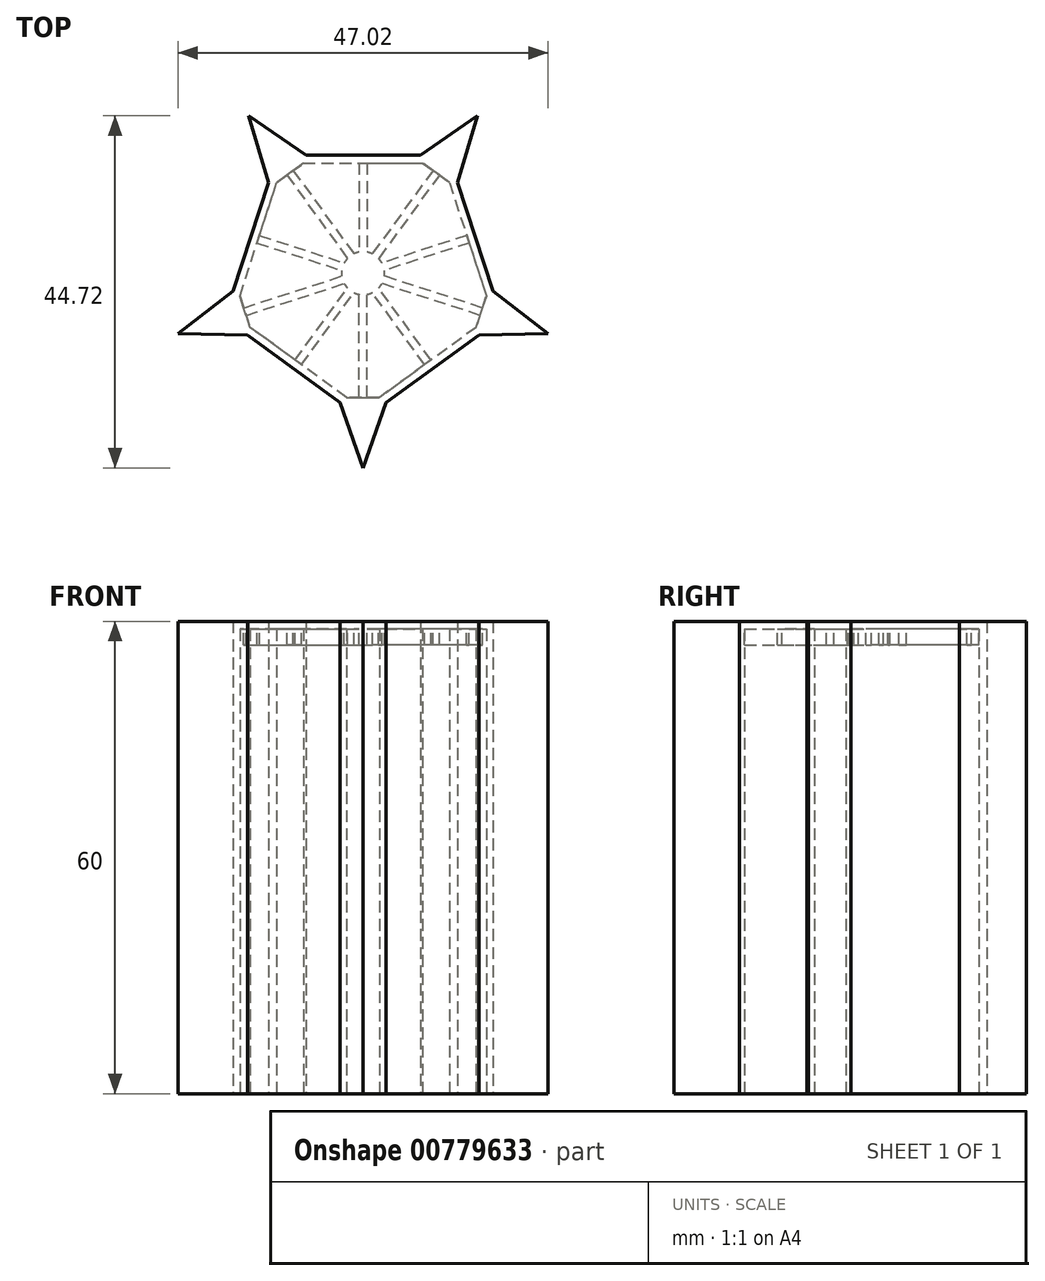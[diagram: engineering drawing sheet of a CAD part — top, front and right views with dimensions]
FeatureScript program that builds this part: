
annotation { "Feature Type Name" : "Feature", "Feature Type Description" : "" }
export const myFeature = defineFeature(function(context is Context, id is Id, definition is map)
    precondition{}
    {
        {
            var Q0;
            Q0=qCreatedBy(makeId("Top.planeOp"),FACE);
            var sketch = newSketch(context, id + "F0", { "sketchPlane" : qUnion([Q0])});
            skCircle(sketch, "E0.cCircle", {"center": v(0, 0) * mm, "radius": 20 * mm, "construction": true});
            skLineSegment(sketch, "E0.0", {"start": v(-14.53, 20) * mm, "end": v(14.53, 20) * mm, "construction": true});
            skLineSegment(sketch, "E0.1", {"start": v(14.53, 20) * mm, "end": v(23.51, -7.64) * mm, "construction": true});
            skLineSegment(sketch, "E0.2", {"start": v(23.51, -7.64) * mm, "end": v(0, -24.72) * mm, "construction": true});
            skLineSegment(sketch, "E0.3", {"start": v(0, -24.72) * mm, "end": v(-23.51, -7.64) * mm, "construction": true});
            skLineSegment(sketch, "E0.4", {"start": v(-23.51, -7.64) * mm, "end": v(-14.53, 20) * mm, "construction": true});
            skPoint(sketch, "E0.0.midPoint", {"position": v(0, 20) * mm});
            skLineSegment(sketch, "E1", {"start": v(-14.53, 20) * mm, "end": v(0, 0) * mm, "construction": true});
            skLineSegment(sketch, "E2", {"start": v(14.53, 20) * mm, "end": v(0, 0) * mm, "construction": true});
            skLineSegment(sketch, "E3", {"start": v(23.51, -7.64) * mm, "end": v(0, 0) * mm, "construction": true});
            skLineSegment(sketch, "E4", {"start": v(0, -24.72) * mm, "end": v(0, 0) * mm, "construction": true});
            skLineSegment(sketch, "E5", {"start": v(-23.51, -7.64) * mm, "end": v(0, 0) * mm, "construction": true});
            skCircle(sketch, "E6.cCircle", {"center": v(0, 0) * mm, "radius": 10 * mm, "construction": true});
            skLineSegment(sketch, "E6.0", {"start": v(-7.27, 10) * mm, "end": v(7.27, 10) * mm, "construction": true});
            skLineSegment(sketch, "E6.1", {"start": v(7.27, 10) * mm, "end": v(11.76, -3.82) * mm, "construction": true});
            skLineSegment(sketch, "E6.2", {"start": v(11.76, -3.82) * mm, "end": v(0, -12.36) * mm, "construction": true});
            skLineSegment(sketch, "E6.3", {"start": v(0, -12.36) * mm, "end": v(-11.76, -3.82) * mm, "construction": true});
            skLineSegment(sketch, "E6.4", {"start": v(-11.76, -3.82) * mm, "end": v(-7.27, 10) * mm, "construction": true});
            skPoint(sketch, "E6.0.midPoint", {"position": v(0, 10) * mm});
            skLineSegment(sketch, "E7", {"start": v(-14.53, 20) * mm, "end": v(-9.51, 3.1) * mm});
            skLineSegment(sketch, "E8", {"start": v(-9.51, 3.1) * mm, "end": v(-23.51, -7.64) * mm});
            skLineSegment(sketch, "E9", {"start": v(-14.53, 20) * mm, "end": v(0, 10) * mm});
            skLineSegment(sketch, "E10", {"start": v(14.53, 20) * mm, "end": v(0, 10) * mm});
            skLineSegment(sketch, "E11", {"start": v(14.53, 20) * mm, "end": v(9.51, 3.1) * mm});
            skLineSegment(sketch, "E12", {"start": v(9.51, 3.1) * mm, "end": v(23.51, -7.64) * mm});
            skLineSegment(sketch, "E13", {"start": v(23.51, -7.64) * mm, "end": v(5.88, -8.1) * mm});
            skLineSegment(sketch, "E14", {"start": v(5.88, -8.1) * mm, "end": v(0, -24.72) * mm});
            skLineSegment(sketch, "E15", {"start": v(-23.51, -7.64) * mm, "end": v(-5.88, -8.1) * mm});
            skLineSegment(sketch, "E16", {"start": v(-5.88, -8.1) * mm, "end": v(0, -24.72) * mm});
            skCircle(sketch, "E17.cCircle", {"center": v(0, 0) * mm, "radius": 15 * mm, "construction": true});
            skLineSegment(sketch, "E17.0", {"start": v(-10.9, 15) * mm, "end": v(10.9, 15) * mm});
            skLineSegment(sketch, "E17.1", {"start": v(10.9, 15) * mm, "end": v(17.63, -5.73) * mm});
            skLineSegment(sketch, "E17.2", {"start": v(17.63, -5.73) * mm, "end": v(0, -18.54) * mm});
            skLineSegment(sketch, "E17.3", {"start": v(0, -18.54) * mm, "end": v(-17.63, -5.73) * mm});
            skLineSegment(sketch, "E17.4", {"start": v(-17.63, -5.73) * mm, "end": v(-10.9, 15) * mm});
            skPoint(sketch, "E17.0.midPoint", {"position": v(0, 15) * mm});
            skPoint(sketch, "E18", {"position": v(7.27, 15) * mm});
            skSolve(sketch);
        }
        {
            var Q0;
            Q0 = qSketchRegion(id + "F0", true);
            extrude(context, id + "F1", {"entities" : qUnion([Q0]), "depth" : 60 * mm, "offsetDistance" : 25 * mm});
        }
        {
            var Q0;
            Q0=makeQuery(id+"F1.opExtrude","CAP_FACE",FACE,{"disambiguationData":[OSD([sQuery(id+"F0.wireOp",EDGE,"E7"),sQuery(id+"F0.wireOp",EDGE,"E8"),sQuery(id+"F0.wireOp",EDGE,"E9"),sQuery(id+"F0.wireOp",EDGE,"E10"),sQuery(id+"F0.wireOp",EDGE,"E11"),sQuery(id+"F0.wireOp",EDGE,"E12"),sQuery(id+"F0.wireOp",EDGE,"E13"),sQuery(id+"F0.wireOp",EDGE,"E14"),sQuery(id+"F0.wireOp",EDGE,"E15"),sQuery(id+"F0.wireOp",EDGE,"E16"),sQuery(id+"F0.wireOp",EDGE,"E17.0"),sQuery(id+"F0.wireOp",EDGE,"E17.1"),sQuery(id+"F0.wireOp",EDGE,"E17.2"),sQuery(id+"F0.wireOp",EDGE,"E17.3"),sQuery(id+"F0.wireOp",EDGE,"E17.4")])],"isStart":true});
            shell(context, id + "F2", {"entities" : qUnion([Q0]), "thickness" : 1 * mm});
        }
        {
            var Q0;
            Q0=makeQuery(id+"F2.opShell","OFFSET_FACE",FACE,{"disambiguationData":[OSD([sQuery(id+"F0.wireOp",EDGE,"E7"),sQuery(id+"F0.wireOp",EDGE,"E8"),sQuery(id+"F0.wireOp",EDGE,"E9"),sQuery(id+"F0.wireOp",EDGE,"E10"),sQuery(id+"F0.wireOp",EDGE,"E11"),sQuery(id+"F0.wireOp",EDGE,"E12"),sQuery(id+"F0.wireOp",EDGE,"E13"),sQuery(id+"F0.wireOp",EDGE,"E14"),sQuery(id+"F0.wireOp",EDGE,"E15"),sQuery(id+"F0.wireOp",EDGE,"E16"),sQuery(id+"F0.wireOp",EDGE,"E17.0"),sQuery(id+"F0.wireOp",EDGE,"E17.1"),sQuery(id+"F0.wireOp",EDGE,"E17.2"),sQuery(id+"F0.wireOp",EDGE,"E17.3"),sQuery(id+"F0.wireOp",EDGE,"E17.4")])]});
            var sketch = newSketch(context, id + "F3", { "sketchPlane" : qUnion([Q0])});
            skLineSegment(sketch, "E19.0", {"start": v(-2.1, 15.78) * mm, "end": v(-14.36, 6.87) * mm});
            skLineSegment(sketch, "E20.0", {"start": v(14.36, 6.87) * mm, "end": v(2.1, 15.78) * mm});
            skLineSegment(sketch, "E21.0", {"start": v(10.97, -11.53) * mm, "end": v(15.66, 2.88) * mm});
            skLineSegment(sketch, "E22.0", {"start": v(-7.58, -14) * mm, "end": v(7.58, -14) * mm});
            skLineSegment(sketch, "E23.0", {"start": v(-15.66, 2.88) * mm, "end": v(-10.97, -11.53) * mm});
            skLineSegment(sketch, "E24", {"start": v(-14.36, 6.87) * mm, "end": v(-15.66, 2.88) * mm});
            skLineSegment(sketch, "E25", {"start": v(-2.1, 15.78) * mm, "end": v(2.1, 15.78) * mm});
            skLineSegment(sketch, "E26", {"start": v(14.36, 6.87) * mm, "end": v(15.66, 2.88) * mm});
            skLineSegment(sketch, "E27", {"start": v(10.97, -11.53) * mm, "end": v(7.58, -14) * mm});
            skLineSegment(sketch, "E28", {"start": v(-7.58, -14) * mm, "end": v(-10.97, -11.53) * mm});
            skSolve(sketch);
        }
        {
            var Q0;
            Q0=makeQuery(id+"F3.imprint","IMPRINT",FACE,{"disambiguationData":[TD([[makeQuery(id+"F3.imprint","IMPRINT",EDGE,{"derivedFrom":sQuery(id+"F3.wireOp",EDGE,"E24")}),-1.0]])]});
            var Q1;
            Q1=makeQuery(id+"F3.imprint","IMPRINT",FACE,{"disambiguationData":[TD([[makeQuery(id+"F3.imprint","IMPRINT",EDGE,{"derivedFrom":sQuery(id+"F3.wireOp",EDGE,"E25")}),1.0]])]});
            var Q2;
            Q2=makeQuery(id+"F3.imprint","IMPRINT",FACE,{"disambiguationData":[TD([[makeQuery(id+"F3.imprint","IMPRINT",EDGE,{"derivedFrom":sQuery(id+"F3.wireOp",EDGE,"E26")}),1.0]])]});
            var Q3;
            Q3=makeQuery(id+"F3.imprint","IMPRINT",FACE,{"disambiguationData":[TD([[makeQuery(id+"F3.imprint","IMPRINT",EDGE,{"derivedFrom":sQuery(id+"F3.wireOp",EDGE,"E27")}),1.0]])]});
            var Q4;
            Q4=makeQuery(id+"F3.imprint","IMPRINT",FACE,{"disambiguationData":[TD([[makeQuery(id+"F3.imprint","IMPRINT",EDGE,{"derivedFrom":sQuery(id+"F3.wireOp",EDGE,"E28")}),1.0]])]});
            var Q5;
            Q5=makeQuery(id+"F1.opExtrude","CAP_FACE",FACE,{"disambiguationData":[OSD([sQuery(id+"F0.wireOp",EDGE,"E7"),sQuery(id+"F0.wireOp",EDGE,"E8"),sQuery(id+"F0.wireOp",EDGE,"E9"),sQuery(id+"F0.wireOp",EDGE,"E10"),sQuery(id+"F0.wireOp",EDGE,"E11"),sQuery(id+"F0.wireOp",EDGE,"E12"),sQuery(id+"F0.wireOp",EDGE,"E13"),sQuery(id+"F0.wireOp",EDGE,"E14"),sQuery(id+"F0.wireOp",EDGE,"E15"),sQuery(id+"F0.wireOp",EDGE,"E16"),sQuery(id+"F0.wireOp",EDGE,"E17.0"),sQuery(id+"F0.wireOp",EDGE,"E17.1"),sQuery(id+"F0.wireOp",EDGE,"E17.2"),sQuery(id+"F0.wireOp",EDGE,"E17.3"),sQuery(id+"F0.wireOp",EDGE,"E17.4")])],"isStart":true});
            extrude(context, id + "F4", {"entities" : qUnion([Q0, Q1, Q2, Q3, Q4]), "operationType" : NewBodyOperationType.ADD, "endBound" : BoundingType.UP_TO_SURFACE, "depth" : 25 * mm, "endBoundEntityFace" : qUnion([Q5]), "offsetDistance" : 25 * mm});
        }
        {
            var Q0;
            Q0=makeQuery(id+"F2.opShell","OFFSET_FACE",FACE,{"disambiguationData":[OSD([sQuery(id+"F0.wireOp",EDGE,"E7"),sQuery(id+"F0.wireOp",EDGE,"E8"),sQuery(id+"F0.wireOp",EDGE,"E9"),sQuery(id+"F0.wireOp",EDGE,"E10"),sQuery(id+"F0.wireOp",EDGE,"E11"),sQuery(id+"F0.wireOp",EDGE,"E12"),sQuery(id+"F0.wireOp",EDGE,"E13"),sQuery(id+"F0.wireOp",EDGE,"E14"),sQuery(id+"F0.wireOp",EDGE,"E15"),sQuery(id+"F0.wireOp",EDGE,"E16"),sQuery(id+"F0.wireOp",EDGE,"E17.0"),sQuery(id+"F0.wireOp",EDGE,"E17.1"),sQuery(id+"F0.wireOp",EDGE,"E17.2"),sQuery(id+"F0.wireOp",EDGE,"E17.3"),sQuery(id+"F0.wireOp",EDGE,"E17.4")])]});
            var sketch = newSketch(context, id + "F5", { "sketchPlane" : qUnion([Q0])});
            skLineSegment(sketch, "E29", {"start": v(13.31, -4.33) * mm, "end": v(0, 0) * mm, "construction": true});
            skLineSegment(sketch, "E30", {"start": v(0, 15.78) * mm, "end": v(0, 0) * mm, "construction": true});
            skLineSegment(sketch, "E31", {"start": v(8.23, 11.33) * mm, "end": v(0, 0) * mm, "construction": true});
            skLineSegment(sketch, "E32", {"start": v(15, 4.88) * mm, "end": v(0, 0) * mm, "construction": true});
            skLineSegment(sketch, "E33", {"start": v(9.27, -12.77) * mm, "end": v(0, 0) * mm, "construction": true});
            skLineSegment(sketch, "E34", {"start": v(-9.27, -12.77) * mm, "end": v(0, 0) * mm, "construction": true});
            skLineSegment(sketch, "E35", {"start": v(0, -14) * mm, "end": v(0, 0) * mm, "construction": true});
            skLineSegment(sketch, "E36", {"start": v(-13.31, -4.33) * mm, "end": v(0, 0) * mm, "construction": true});
            skLineSegment(sketch, "E37", {"start": v(-15, 4.88) * mm, "end": v(0, 0) * mm, "construction": true});
            skLineSegment(sketch, "E38", {"start": v(-8.23, 11.33) * mm, "end": v(0, 0) * mm, "construction": true});
            skLineSegment(sketch, "E39.0", {"start": v(-14.85, 5.35) * mm, "end": v(-1.3, 0.95) * mm});
            skLineSegment(sketch, "E40.0", {"start": v(-15.16, 4.4) * mm, "end": v(-1.62, 0) * mm});
            skLineSegment(sketch, "E41.0", {"start": v(-13.16, -4.8) * mm, "end": v(-1.3, -0.95) * mm});
            skLineSegment(sketch, "E42.0", {"start": v(-13.47, -3.85) * mm, "end": v(-1.62, 0) * mm});
            skLineSegment(sketch, "E43.0", {"start": v(-8.87, -13.06) * mm, "end": v(-0.5, -1.54) * mm});
            skLineSegment(sketch, "E44.0", {"start": v(-9.68, -12.47) * mm, "end": v(-1.3, -0.95) * mm});
            skLineSegment(sketch, "E45.0", {"start": v(0.5, -14) * mm, "end": v(0.5, -1.54) * mm});
            skLineSegment(sketch, "E46.0", {"start": v(-0.5, -14) * mm, "end": v(-0.5, -1.54) * mm});
            skLineSegment(sketch, "E47.0", {"start": v(9.68, -12.47) * mm, "end": v(1.3, -0.95) * mm});
            skLineSegment(sketch, "E48.0", {"start": v(8.87, -13.06) * mm, "end": v(0.5, -1.54) * mm});
            skLineSegment(sketch, "E49.0", {"start": v(13.47, -3.85) * mm, "end": v(1.62, 0) * mm});
            skLineSegment(sketch, "E50.0", {"start": v(13.16, -4.8) * mm, "end": v(1.3, -0.95) * mm});
            skLineSegment(sketch, "E51.0", {"start": v(14.85, 5.35) * mm, "end": v(1.3, 0.95) * mm});
            skLineSegment(sketch, "E52.0", {"start": v(15.16, 4.4) * mm, "end": v(1.62, 0) * mm});
            skLineSegment(sketch, "E53.0", {"start": v(7.82, 11.62) * mm, "end": v(0.5, 1.54) * mm});
            skLineSegment(sketch, "E54.0", {"start": v(8.63, 11.03) * mm, "end": v(1.3, 0.95) * mm});
            skLineSegment(sketch, "E55.0", {"start": v(-0.5, 15.78) * mm, "end": v(-0.5, 1.54) * mm});
            skLineSegment(sketch, "E56.0", {"start": v(0.5, 15.78) * mm, "end": v(0.5, 1.54) * mm});
            skLineSegment(sketch, "E57.0", {"start": v(-8.63, 11.03) * mm, "end": v(-1.3, 0.95) * mm});
            skLineSegment(sketch, "E58.0", {"start": v(-7.82, 11.62) * mm, "end": v(-0.5, 1.54) * mm});
            skCircle(sketch, "E59", {"center": v(0, 0) * mm, "radius": 2.73 * mm});
            skSolve(sketch);
        }
        {
            var Q0;
            Q0 = qSketchRegion(id + "F5", true);
            var Q1;
            {var subQ0=sQuery(id+"F5.wireOp",EDGE,"E39.0");var subQ1=makeQuery(id+"F4.opExtrude","CAP_EDGE",EDGE,{"disambiguationData":[OSD([sQuery(id+"F3.wireOp",EDGE,"E24")])],"isStart":true});var subQ2=makeQuery(id+"F5.imprint","INTERSECT",VERTEX,{"derivedFrom":[subQ1,subQ0]});Q1=makeQuery(id+"F5.imprint","IMPRINT",FACE,{"disambiguationData":[TD([[makeQuery(id+"F5.imprint","IMPRINT",EDGE,{"disambiguationData":[TD([[subQ2,-1.0]])],"derivedFrom":subQ0}),-1.0]])]});}
            var Q2;
            {var subQ0=sQuery(id+"F5.wireOp",EDGE,"E57.0");var subQ4=sQuery(id+"F5.wireOp",EDGE,"E59");var subQ5=makeQuery(id+"F5.imprint","INTERSECT",VERTEX,{"derivedFrom":[subQ0,subQ4]});Q2=makeQuery(id+"F5.imprint","IMPRINT",FACE,{"disambiguationData":[TD([[makeQuery(id+"F5.imprint","IMPRINT",EDGE,{"disambiguationData":[TD([[subQ5,1.0]])],"derivedFrom":subQ4}),-1.0]])]});}
            var Q3;
            {var subQ0=sQuery(id+"F5.wireOp",EDGE,"E55.0");var subQ1=makeQuery(id+"F4.opExtrude","CAP_EDGE",EDGE,{"disambiguationData":[OSD([sQuery(id+"F3.wireOp",EDGE,"E25")])],"isStart":true});var subQ2=makeQuery(id+"F5.imprint","INTERSECT",VERTEX,{"derivedFrom":[subQ1,subQ0]});Q3=makeQuery(id+"F5.imprint","IMPRINT",FACE,{"disambiguationData":[TD([[makeQuery(id+"F5.imprint","IMPRINT",EDGE,{"disambiguationData":[TD([[subQ2,-1.0]])],"derivedFrom":subQ0}),1.0]])]});}
            var Q4;
            {var subQ0=sQuery(id+"F5.wireOp",EDGE,"E53.0");var subQ4=sQuery(id+"F5.wireOp",EDGE,"E59");var subQ5=makeQuery(id+"F5.imprint","INTERSECT",VERTEX,{"derivedFrom":[subQ0,subQ4]});Q4=makeQuery(id+"F5.imprint","IMPRINT",FACE,{"disambiguationData":[TD([[makeQuery(id+"F5.imprint","IMPRINT",EDGE,{"disambiguationData":[TD([[subQ5,1.0]])],"derivedFrom":subQ4}),-1.0]])]});}
            var Q5;
            {var subQ0=sQuery(id+"F5.wireOp",EDGE,"E51.0");var subQ1=makeQuery(id+"F4.opExtrude","CAP_EDGE",EDGE,{"disambiguationData":[OSD([sQuery(id+"F3.wireOp",EDGE,"E26")])],"isStart":true});var subQ2=makeQuery(id+"F5.imprint","INTERSECT",VERTEX,{"derivedFrom":[subQ1,subQ0]});Q5=makeQuery(id+"F5.imprint","IMPRINT",FACE,{"disambiguationData":[TD([[makeQuery(id+"F5.imprint","IMPRINT",EDGE,{"disambiguationData":[TD([[subQ2,-1.0]])],"derivedFrom":subQ0}),1.0]])]});}
            var Q6;
            {var subQ0=sQuery(id+"F5.wireOp",EDGE,"E49.0");var subQ4=sQuery(id+"F5.wireOp",EDGE,"E59");var subQ5=makeQuery(id+"F5.imprint","INTERSECT",VERTEX,{"derivedFrom":[subQ0,subQ4]});Q6=makeQuery(id+"F5.imprint","IMPRINT",FACE,{"disambiguationData":[TD([[makeQuery(id+"F5.imprint","IMPRINT",EDGE,{"disambiguationData":[TD([[subQ5,1.0]])],"derivedFrom":subQ4}),-1.0]])]});}
            var Q7;
            {var subQ0=sQuery(id+"F5.wireOp",EDGE,"E47.0");var subQ1=makeQuery(id+"F4.opExtrude","CAP_EDGE",EDGE,{"disambiguationData":[OSD([sQuery(id+"F3.wireOp",EDGE,"E27")])],"isStart":true});var subQ2=makeQuery(id+"F5.imprint","INTERSECT",VERTEX,{"derivedFrom":[subQ1,subQ0]});Q7=makeQuery(id+"F5.imprint","IMPRINT",FACE,{"disambiguationData":[TD([[makeQuery(id+"F5.imprint","IMPRINT",EDGE,{"disambiguationData":[TD([[subQ2,-1.0]])],"derivedFrom":subQ0}),1.0]])]});}
            var Q8;
            {var subQ0=sQuery(id+"F5.wireOp",EDGE,"E45.0");var subQ4=sQuery(id+"F5.wireOp",EDGE,"E59");var subQ5=makeQuery(id+"F5.imprint","INTERSECT",VERTEX,{"derivedFrom":[subQ0,subQ4]});Q8=makeQuery(id+"F5.imprint","IMPRINT",FACE,{"disambiguationData":[TD([[makeQuery(id+"F5.imprint","IMPRINT",EDGE,{"disambiguationData":[TD([[subQ5,1.0]])],"derivedFrom":subQ4}),-1.0]])]});}
            var Q9;
            {var subQ0=sQuery(id+"F5.wireOp",EDGE,"E43.0");var subQ1=makeQuery(id+"F4.opExtrude","CAP_EDGE",EDGE,{"disambiguationData":[OSD([sQuery(id+"F3.wireOp",EDGE,"E28")])],"isStart":true});var subQ2=makeQuery(id+"F5.imprint","INTERSECT",VERTEX,{"derivedFrom":[subQ1,subQ0]});Q9=makeQuery(id+"F5.imprint","IMPRINT",FACE,{"disambiguationData":[TD([[makeQuery(id+"F5.imprint","IMPRINT",EDGE,{"disambiguationData":[TD([[subQ2,-1.0]])],"derivedFrom":subQ0}),1.0]])]});}
            var Q10;
            {var subQ0=sQuery(id+"F5.wireOp",EDGE,"E41.0");var subQ4=sQuery(id+"F5.wireOp",EDGE,"E59");var subQ5=makeQuery(id+"F5.imprint","INTERSECT",VERTEX,{"derivedFrom":[subQ0,subQ4]});Q10=makeQuery(id+"F5.imprint","IMPRINT",FACE,{"disambiguationData":[TD([[makeQuery(id+"F5.imprint","IMPRINT",EDGE,{"disambiguationData":[TD([[subQ5,1.0]])],"derivedFrom":subQ4}),-1.0]])]});}
            extrude(context, id + "F6", {"entities" : qUnion([Q0, Q1, Q2, Q3, Q4, Q5, Q6, Q7, Q8, Q9, Q10]), "operationType" : NewBodyOperationType.ADD, "depth" : 2 * mm, "offsetDistance" : 25 * mm});
        }
    });
